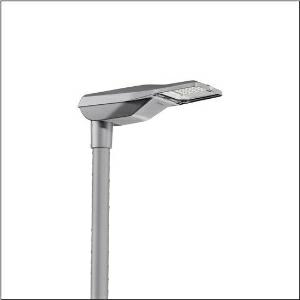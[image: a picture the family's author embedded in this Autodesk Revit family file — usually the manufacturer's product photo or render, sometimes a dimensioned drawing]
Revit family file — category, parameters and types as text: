
# Revit family: streetlight_sl_21_iq_micro___st1_0ab_5xe1m31d08cb_a4c0
name_source: partatom
category: Lighting Fixtures
units: mm (PartAtom-declared; Revit-internal decimal feet)

## family parameters
Cut with Voids When Loaded = No
Host = Face
Light Source = No
Part Type = Normal
Room Calculation Point = No
Round Connector Dimension = Use Diameter
Shared = No

## types (1)
- --- (1 x LED, 2520 lm, 19.4 W, 3000K)
    Apparent Load = 19 VA
    CIE Flux Codes = 38 73 97 100 100
    Color Rendering = 70
    Color Temperature = 3000K
    Default Elevation = 1800 mm
    Description = Streetlight SL 21 iQ micro, mast luminaire, primary light control with lens, of PMMA, primary optical cover: cover, of toughened safety glass, transparent, light distribution: ST1.0aB, light emission: direct distribution, primary light characteristic: asymmetric, installation type: post-top, side-entry, LED, High Power LED, rated luminous flux: 2.520lm, luminous efficacy: 130lm/W, light colour: 730, colour temperature: 3000K, control gear: iQ-Comfort, control: Auto-Match, Temp-Guard, Lumen-Switch, Night-Set, Smart-Wire, Light-Fading, Desk-Remote (wireless, voltage-free reading and setting of iQ features in the workshop via application-optimized NFC function/RFID function), optimised constant luminous flux control (CLO 2.0), pre-setting: linear dimming characteristic, mains connection: 220..240V, AC, 50/60Hz, start of lifetime: 19W, end of service life: 20W, reduction: 10W, luminaire housing, of diecast aluminium, powder-coated, Siteco® metallic grey (DB 702S), corrosivity category C5 mid according to DIN EN ISO 12944, please order mast flange separately, inclination adjustable: 0°, 5°, 10°, 15°, sealing non-destructively replaceable, multi-level sealing system, length: 528mm, width: 235mm, height: 110mm, mast flange for spigot size: 42mm (side-entry): 5XC10008XM4, 60/48mm (side-entry/post-top): 5XC10108XM2, 76/60mm (side-entry/post-top): 5XC10108XM1, protection rating (complete): IP66, insulation class (complete): insulation class II (safety insulation), certification: CE, ENEC, ENEC+, VDE, impact resistance: IK10, permissible operating ambient temperature for outdoor applications: -40..+50°C, standard-compliant lighting for roads and squares, packaging unit: 1 piece

Light Distribution: ST1.0aB
    Height = 110 mm
    Lamp = 1 x LED
    Lamp Light Flux = 2520 lm
    Lamp Power = 19.4 W
    Lamp count = 1
    Length = 528 mm
    Luminous efficacy = 130 lm/W
    Manufacturer = Siteco
    ModVariant = No
    Model = 5XE1M31D08CB
    Number of Poles = 1
    OnlyDefault = Yes
    Power Factor = 1
    Product Name = Streetlight SL 21 iQ micro | ST1.0aB
    Product group = mast luminaire | pylon top
    ProductGroupID = 6100
    Protection Class = Protection class II
    Protection Degree = IP 66
    RLX_Detail_Level = 1
    RLX_Emergency_Light_Flux = 0 lm
    RLX_Emergency_Type = 0
    RLX_Emergency_Type_DB = No
    RlxData = <blob elided: 98657 chars, md5=bc944dae>
    Socket = socket
    Standby Power = 0 W
    System Light Flux = 2520 lm
    System Power = 19 W
    Type Comments = factory setting: luminous flux: 100 % | dim-lin: 254 | 387 mA
    Type Image = l_1006881.jpg
    URL = http://relux.com
    VarID = @adj_138180
    Voltage = 0 V
    Weight = 0.00 kg
    Width = 235 mm

## geometry (parser evidence)
native form markers: Blend x4, Sweep x10
no freeform markers — native parametric forms only
